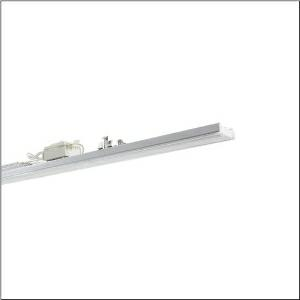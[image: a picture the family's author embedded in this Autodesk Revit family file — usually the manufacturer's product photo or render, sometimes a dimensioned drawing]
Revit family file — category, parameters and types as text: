
# Revit family: licross_21_recessed_ho_52tl11dn4axs
name_source: partatom
category: Lighting Fixtures
units: mm (PartAtom-declared; Revit-internal decimal feet)

## family parameters
Cut with Voids When Loaded = No
Host = Face
Light Source = No
Part Type = Normal
Room Calculation Point = No
Round Connector Dimension = Use Diameter
Shared = No

## types (1)
- --- (1 x LED, 10000 lm, 54.7 W, 4000K)
    Apparent Load = 55 VA
    CIE Flux Codes = 87 95 99 100 100
    Color Rendering = 80
    Color Temperature = 4000K
    Default Elevation = 1800 mm
    Description = Licross 21 Recessed HO, luminaire insert, of sheet steel, galvanised, coil coated, white, length: 1.500mm, width: 66mm, height: 67mm, LED rated luminous flux: 10.000lm, light colour: 840, SDCM (Standard Deviation of Colour Matching)MacAdam ≤ 3 SDCM (initial), control gear: DALI 2, with plug, 5-pole, with phase selection, mains connection: 220..240V, AC, 50/60Hz, rated input power: 55W, internal wiring halogen-free, primary light control with lens, of plastic, primary optical cover: cover, of PMMA, light emission: direct distribution, primary light characteristic: symmetric, protection rating (complete): IP40, insulation class (complete): insulation class I (protective earthing), certification: CE, ENEC, VDE, UKCA, protection symbol: D if used in an environment without relevant dust loads with corresponding accessories, impact resistance: IK06, permissible ambient temperature for indoor applications: -25..+40°C, corresponds to IFS (International Featured Standards) requirements for safety and quality in the food industry, reducing of maximum allowable ambient temperature of 5°C with ceiling mounting, LABS conformity tested according to VDMA 24364:2018-05, The light source and the operating device comply with the requirements of the Ecodesign Regulation (EU) 2019/2020 and are replaceable in accordance with this regulation, packaging unit: 1 piece
    Height = 58 mm
    Lamp = 1 x LED
    Lamp Light Flux = 10000 lm
    Lamp Power = 54.7 W
    Lamp count = 1
    Length = 1500 mm
    Luminous efficacy = 183 lm/W
    Manufacturer = Siteco
    ModVariant = No
    Model = 52TL11DN4AXS
    Mounting Place = Ceiling
    Mounting Type = Pendant
    Number of Poles = 1
    OnlyDefault = Yes
    Power Factor = 1
    Product Name = Licross 21 Recessed HO
    Product group = luminaire insert | ceiling pendant
    ProductGroupID = 901
    Protection Class = Protection class I
    Protection Degree = IP 40
    RLX_Detail_Level = 1
    RLX_Emergency_Light_Flux = 0 lm
    RLX_Emergency_Type = 0
    RLX_Emergency_Type_DB = No
    RlxData = <blob elided: 24649 chars, md5=b01717a1>
    Socket = socket
    Standby Power = 0 W
    System Light Flux = 10000 lm
    System Power = 55 W
    Type Comments = factory setting: luminous flux: 100 % | dim-lin: 254 | 313 mA
    Type Image = l_1296930.jpg
    URL = http://relux.com
    VarID = @adj_127421
    Voltage = 0 V
    Weight = 0.00 kg
    Width = 66 mm

## geometry (parser evidence)
native form markers: Blend x4, Sweep x13
no freeform markers — native parametric forms only
